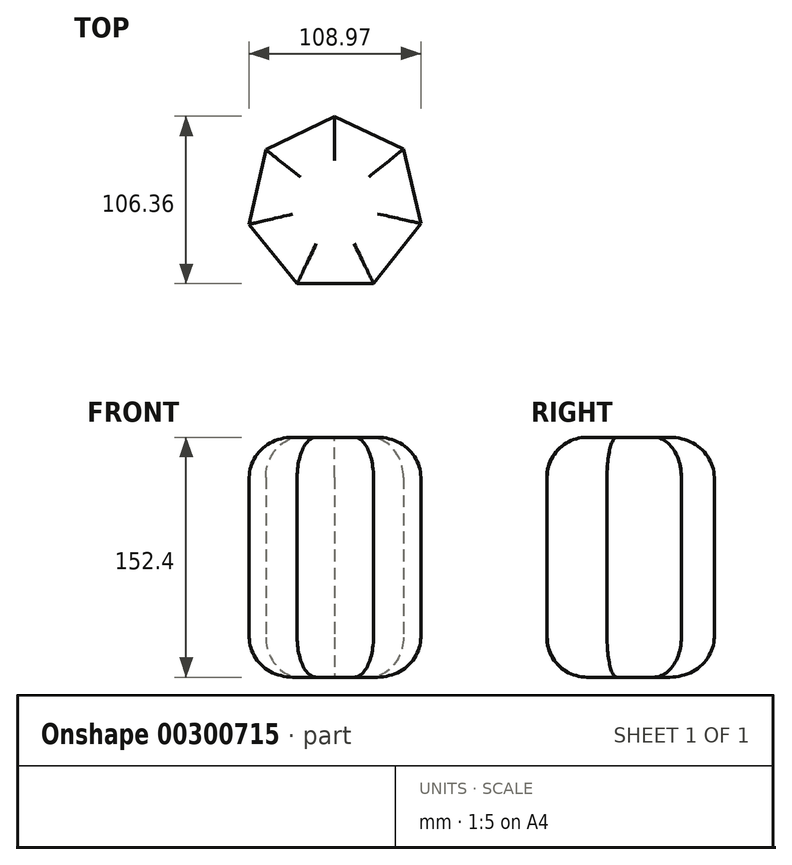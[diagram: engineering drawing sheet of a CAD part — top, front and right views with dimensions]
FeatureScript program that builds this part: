
annotation { "Feature Type Name" : "Feature", "Feature Type Description" : "" }
export const myFeature = defineFeature(function(context is Context, id is Id, definition is map)
    precondition{}
    {
        {
            var Q0;
            Q0=qCreatedBy(makeId("Top.planeOp"),FACE);
            var sketch = newSketch(context, id + "F0", { "sketchPlane" : qUnion([Q0])});
            skCircle(sketch, "E0", {"center": v(0, 0) * mm, "radius": 55.89 * mm});
            skPoint(sketch, "E1", {"position": v(0, 55.89) * mm});
            skPoint(sketch, "E2", {"position": v(55.89, 0) * mm});
            skPoint(sketch, "E3", {"position": v(-55.89, 0) * mm});
            skPoint(sketch, "E4", {"position": v(0, -55.89) * mm});
            skCircle(sketch, "E5.cCircle", {"center": v(0, 0) * mm, "radius": 55.89 * mm, "construction": true});
            skLineSegment(sketch, "E5.0", {"start": v(43.53, 35.05) * mm, "end": v(54.54, -12.18) * mm});
            skLineSegment(sketch, "E5.1", {"start": v(54.54, -12.18) * mm, "end": v(24.49, -50.24) * mm});
            skLineSegment(sketch, "E5.2", {"start": v(24.49, -50.24) * mm, "end": v(-24, -50.47) * mm});
            skLineSegment(sketch, "E5.3", {"start": v(-24, -50.47) * mm, "end": v(-54.43, -12.7) * mm});
            skLineSegment(sketch, "E5.4", {"start": v(-54.43, -12.7) * mm, "end": v(-43.86, 34.64) * mm});
            skLineSegment(sketch, "E5.5", {"start": v(-43.86, 34.64) * mm, "end": v(-0.27, 55.89) * mm});
            skLineSegment(sketch, "E5.6", {"start": v(-0.27, 55.89) * mm, "end": v(43.53, 35.05) * mm});
            skLineSegment(sketch, "E6", {"start": v(0, 0) * mm, "end": v(-43.86, 34.64) * mm});
            skLineSegment(sketch, "E7", {"start": v(0, 0) * mm, "end": v(0, 55.89) * mm});
            skLineSegment(sketch, "E8", {"start": v(0, 0) * mm, "end": v(43.53, 35.05) * mm});
            skLineSegment(sketch, "E9", {"start": v(0, 0) * mm, "end": v(54.54, -12.18) * mm});
            skLineSegment(sketch, "E10", {"start": v(0, 0) * mm, "end": v(-55.89, 0) * mm});
            skLineSegment(sketch, "E11", {"start": v(0, 0) * mm, "end": v(0, -55.89) * mm});
            skLineSegment(sketch, "E12", {"start": v(0, 0) * mm, "end": v(-54.43, -12.7) * mm});
            skLineSegment(sketch, "E13", {"start": v(0, 0) * mm, "end": v(55.89, 0) * mm});
            skLineSegment(sketch, "E14", {"start": v(0, 0) * mm, "end": v(24.49, -50.24) * mm});
            skLineSegment(sketch, "E15", {"start": v(0, 0) * mm, "end": v(-24, -50.47) * mm});
            skSolve(sketch);
        }
        {
            var Q0;
            {var subQ0=sQuery(id+"F0.wireOp",EDGE,"E5.5");Q0=makeQuery(id+"F0.imprint","IMPRINT",FACE,{"disambiguationData":[TD([[makeQuery(id+"F0.imprint","IMPRINT",EDGE,{"derivedFrom":subQ0}),-1.0]])]});}
            var Q1;
            {var subQ0=sQuery(id+"F0.wireOp",EDGE,"E8");Q1=makeQuery(id+"F0.imprint","IMPRINT",FACE,{"disambiguationData":[TD([[makeQuery(id+"F0.imprint","IMPRINT",EDGE,{"derivedFrom":subQ0}),1.0]])]});}
            var Q2;
            {var subQ0=sQuery(id+"F0.wireOp",EDGE,"E8");Q2=makeQuery(id+"F0.imprint","IMPRINT",FACE,{"disambiguationData":[TD([[makeQuery(id+"F0.imprint","IMPRINT",EDGE,{"derivedFrom":subQ0}),-1.0]])]});}
            var Q3;
            Q3=makeQuery(id+"F0.imprint","IMPRINT",FACE,{"disambiguationData":[TD([[makeQuery(id+"F0.imprint","IMPRINT",EDGE,{"derivedFrom":sQuery(id+"F0.wireOp",EDGE,"E5.1")}),-1.0]])]});
            var Q4;
            {var subQ0=sQuery(id+"F0.wireOp",EDGE,"E15");Q4=makeQuery(id+"F0.imprint","IMPRINT",FACE,{"disambiguationData":[TD([[makeQuery(id+"F0.imprint","IMPRINT",EDGE,{"derivedFrom":subQ0}),1.0]])]});}
            var Q5;
            {var subQ0=sQuery(id+"F0.wireOp",EDGE,"E14");Q5=makeQuery(id+"F0.imprint","IMPRINT",FACE,{"disambiguationData":[TD([[makeQuery(id+"F0.imprint","IMPRINT",EDGE,{"derivedFrom":subQ0}),-1.0]])]});}
            var Q6;
            Q6=makeQuery(id+"F0.imprint","IMPRINT",FACE,{"disambiguationData":[TD([[makeQuery(id+"F0.imprint","IMPRINT",EDGE,{"derivedFrom":sQuery(id+"F0.wireOp",EDGE,"E5.3")}),-1.0]])]});
            var Q7;
            {var subQ0=sQuery(id+"F0.wireOp",EDGE,"E6");Q7=makeQuery(id+"F0.imprint","IMPRINT",FACE,{"disambiguationData":[TD([[makeQuery(id+"F0.imprint","IMPRINT",EDGE,{"derivedFrom":subQ0}),1.0]])]});}
            var Q8;
            {var subQ0=sQuery(id+"F0.wireOp",EDGE,"E12");Q8=makeQuery(id+"F0.imprint","IMPRINT",FACE,{"disambiguationData":[TD([[makeQuery(id+"F0.imprint","IMPRINT",EDGE,{"derivedFrom":subQ0}),-1.0]])]});}
            var Q9;
            {var subQ0=sQuery(id+"F0.wireOp",EDGE,"E9");Q9=makeQuery(id+"F0.imprint","IMPRINT",FACE,{"disambiguationData":[TD([[makeQuery(id+"F0.imprint","IMPRINT",EDGE,{"derivedFrom":subQ0}),1.0]])]});}
            extrude(context, id + "F1", {"entities" : qUnion([Q0, Q1, Q2, Q3, Q4, Q5, Q6, Q7, Q8, Q9]), "endBound" : BoundingType.SYMMETRIC, "depth" : 152.4 * mm});
        }
        {
            var Q0;
            Q0=makeQuery(id+"F1.opExtrude","CAP_FACE",FACE,{"disambiguationData":[OSD([sQuery(id+"F0.wireOp",EDGE,"E5.0"),sQuery(id+"F0.wireOp",EDGE,"E5.1"),sQuery(id+"F0.wireOp",EDGE,"E5.2"),sQuery(id+"F0.wireOp",EDGE,"E5.3"),sQuery(id+"F0.wireOp",EDGE,"E5.4"),sQuery(id+"F0.wireOp",EDGE,"E5.5"),sQuery(id+"F0.wireOp",EDGE,"E5.6")])],"isStart":true});
            var Q1;
            Q1=makeQuery(id+"F1.opExtrude","CAP_FACE",FACE,{"disambiguationData":[OSD([sQuery(id+"F0.wireOp",EDGE,"E5.0"),sQuery(id+"F0.wireOp",EDGE,"E5.1"),sQuery(id+"F0.wireOp",EDGE,"E5.2"),sQuery(id+"F0.wireOp",EDGE,"E5.3"),sQuery(id+"F0.wireOp",EDGE,"E5.4"),sQuery(id+"F0.wireOp",EDGE,"E5.5"),sQuery(id+"F0.wireOp",EDGE,"E5.6")])],"isStart":false});
            fillet(context, id + "F2", {"entities" : qUnion([Q0, Q1]), "radius" : 25.4 * mm, "tangentPropagation" : true, "allowEdgeOverflow" : false});
        }
    });
